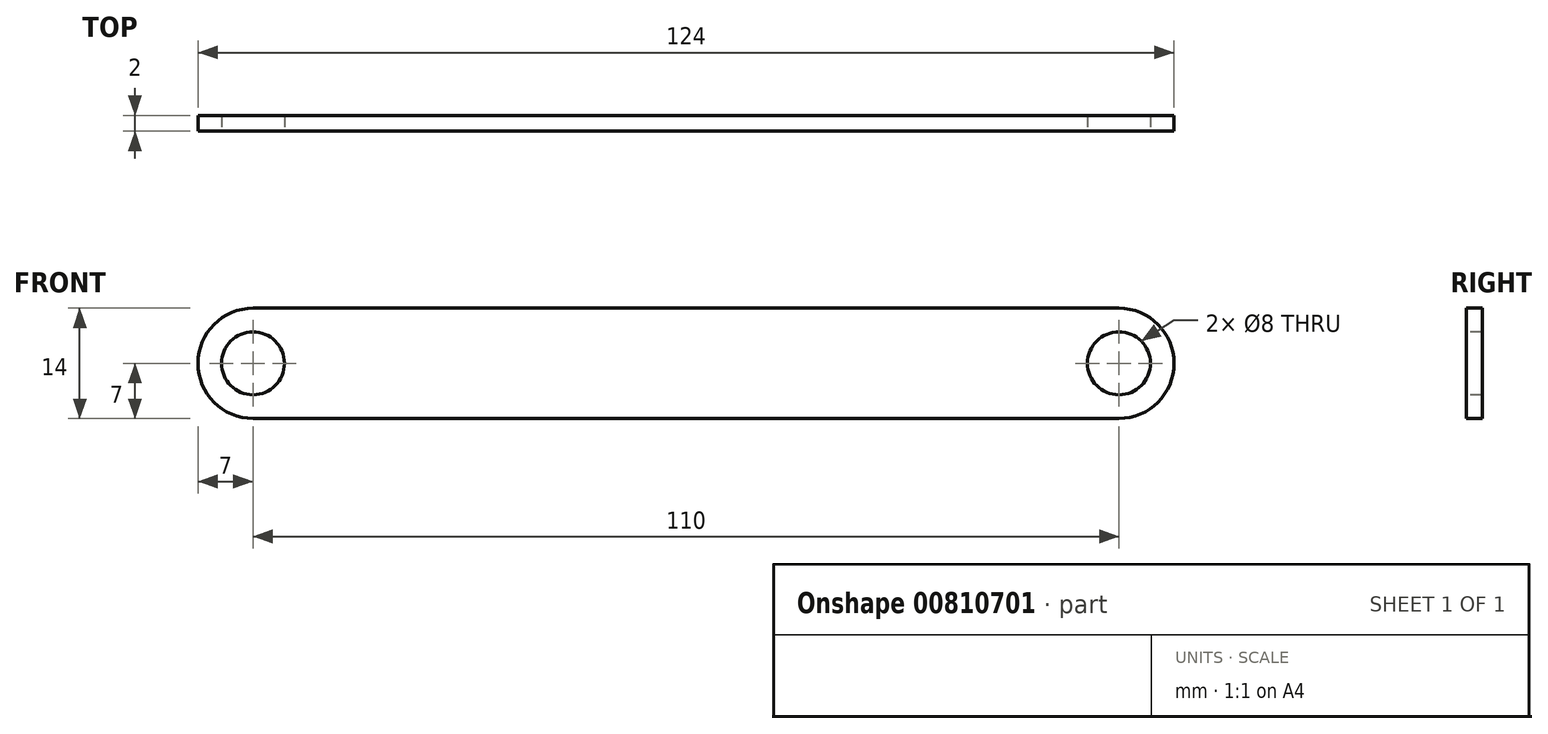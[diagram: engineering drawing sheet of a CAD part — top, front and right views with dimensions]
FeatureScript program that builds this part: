
annotation { "Feature Type Name" : "Feature", "Feature Type Description" : "" }
export const myFeature = defineFeature(function(context is Context, id is Id, definition is map)
    precondition{}
    {
        {
            var Q0;
            Q0=qCreatedBy(makeId("Front.planeOp"),FACE);
            var sketch = newSketch(context, id + "F0", { "sketchPlane" : qUnion([Q0])});
            skLineSegment(sketch, "E0.bottom", {"start": v(-62, 7) * mm, "end": v(62, 7) * mm});
            skLineSegment(sketch, "E0.top", {"start": v(-62, -7) * mm, "end": v(62, -7) * mm});
            skLineSegment(sketch, "E0.left", {"start": v(-62, 7) * mm, "end": v(-62, -7) * mm});
            skLineSegment(sketch, "E0.right", {"start": v(62, 7) * mm, "end": v(62, -7) * mm});
            skSolve(sketch);
        }
        {
            var Q0;
            Q0=makeQuery(id+"F0.imprint","IMPRINT",FACE,{"disambiguationData":[TD([[makeQuery(id+"F0.imprint","IMPRINT",EDGE,{"derivedFrom":sQuery(id+"F0.wireOp",EDGE,"E0.bottom")}),-1.0]])]});
            extrude(context, id + "F1", {"entities" : qUnion([Q0]), "depth" : 2 * mm, "offsetDistance" : 25 * mm});
        }
        {
            var Q0;
            Q0=makeQuery(id+"F1.opExtrude","CAP_FACE",FACE,{"disambiguationData":[OSD([sQuery(id+"F0.wireOp",EDGE,"E0.bottom"),sQuery(id+"F0.wireOp",EDGE,"E0.top"),sQuery(id+"F0.wireOp",EDGE,"E0.left"),sQuery(id+"F0.wireOp",EDGE,"E0.right")])],"isStart":false});
            var sketch = newSketch(context, id + "F2", { "sketchPlane" : qUnion([Q0])});
            skLineSegment(sketch, "E1", {"start": v(-55, 6.4) * mm, "end": v(-55, -7.79) * mm, "construction": true});
            skLineSegment(sketch, "E2", {"start": v(55, 8.19) * mm, "end": v(55, -8.34) * mm, "construction": true});
            skCircle(sketch, "E3", {"center": v(-55, 0) * mm, "radius": 4 * mm});
            skCircle(sketch, "E4", {"center": v(55, 0) * mm, "radius": 4 * mm});
            skSolve(sketch);
        }
        {
            var Q0;
            Q0=makeQuery(id+"F2.imprint","IMPRINT",FACE,{"disambiguationData":[TD([[makeQuery(id+"F2.imprint","IMPRINT",EDGE,{"derivedFrom":sQuery(id+"F2.wireOp",EDGE,"E3")}),1.0]])]});
            extrude(context, id + "F3", {"entities" : qUnion([Q0]), "operationType" : NewBodyOperationType.REMOVE, "oppositeDirection" : true, "depth" : 25 * mm, "offsetDistance" : 25 * mm});
        }
        {
            var Q0;
            Q0=makeQuery(id+"F1.opExtrude","CAP_FACE",FACE,{"disambiguationData":[OSD([sQuery(id+"F0.wireOp",EDGE,"E0.bottom"),sQuery(id+"F0.wireOp",EDGE,"E0.top"),sQuery(id+"F0.wireOp",EDGE,"E0.left"),sQuery(id+"F0.wireOp",EDGE,"E0.right")])],"isStart":false});
            var sketch = newSketch(context, id + "F4", { "sketchPlane" : qUnion([Q0])});
            skLineSegment(sketch, "E5", {"start": v(55, 8.15) * mm, "end": v(55, -10.14) * mm, "construction": true});
            skCircle(sketch, "E6", {"center": v(55, 0) * mm, "radius": 4 * mm});
            skSolve(sketch);
        }
        {
            var Q0;
            Q0 = qSketchRegion(id + "F4", true);
            extrude(context, id + "F5", {"entities" : qUnion([Q0]), "operationType" : NewBodyOperationType.REMOVE, "oppositeDirection" : true, "depth" : 25 * mm, "offsetDistance" : 25 * mm});
        }
        {
            var Q0;
            Q0=makeQuery(id+"F1.opExtrude","SWEPT_EDGE",EDGE,{"disambiguationData":[OSD([sQuery(id+"F0.wireOp",EDGE,"E0.bottom"),sQuery(id+"F0.wireOp",EDGE,"E0.left")])]});
            var Q1;
            Q1=makeQuery(id+"F1.opExtrude","SWEPT_EDGE",EDGE,{"disambiguationData":[OSD([sQuery(id+"F0.wireOp",EDGE,"E0.top"),sQuery(id+"F0.wireOp",EDGE,"E0.left")])]});
            var Q2;
            Q2=makeQuery(id+"F1.opExtrude","SWEPT_EDGE",EDGE,{"disambiguationData":[OSD([sQuery(id+"F0.wireOp",EDGE,"E0.bottom"),sQuery(id+"F0.wireOp",EDGE,"E0.right")])]});
            var Q3;
            Q3=makeQuery(id+"F1.opExtrude","SWEPT_EDGE",EDGE,{"disambiguationData":[OSD([sQuery(id+"F0.wireOp",EDGE,"E0.top"),sQuery(id+"F0.wireOp",EDGE,"E0.right")])]});
            fillet(context, id + "F6", {"entities" : qUnion([Q0, Q1, Q2, Q3]), "radius" : 7 * mm, "tangentPropagation" : true, "allowEdgeOverflow" : false});
        }
    });
